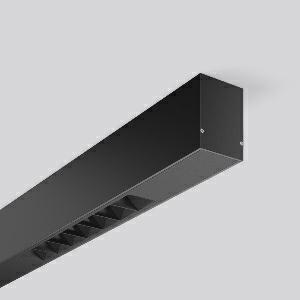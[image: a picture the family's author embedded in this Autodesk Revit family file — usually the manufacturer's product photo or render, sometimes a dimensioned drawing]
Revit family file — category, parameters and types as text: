
# Revit family: less_is_more_beamline_312488_003_3083
name_source: partatom
category: Lighting Fixtures
units: mm (PartAtom-declared; Revit-internal decimal feet)

## family parameters
Cut with Voids When Loaded = No
Host = Face
Light Source = No
Part Type = Normal
Room Calculation Point = No
Round Connector Dimension = Use Diameter
Shared = No

## types (1)
- LESS IS MORE BEAMLINE (1 x LED Modul 930, 1825 lm, 3000)
    Apparent Load = 48 VA
    CIE Flux Codes = 100 100 100 100 100
    Color Rendering = 90
    Color Temperature = 3000
    Default Elevation = 1800 mm
    Description = Series: LESS IS MORE BEAMLINE
Linear ceiling and wall luminaire for aesthetically sophisticated lighting. Luminaire with two LED light units. Housing: extruded aluminium profile, powder-coated. End cap aluminium powder-coated. LED light unit with MRS technology: Mini-Reflector-System made of metallised thermoplastic with prismatic black glare-suppressing frame for pleasant glare-free light (RUG < 10). Each LED light unit has 7 reflector elements. Wide beam light distribution. LED unit with integrated converter interchangeable and removable. Suitable for through-wiring. 
Colour: deep black, matt (RAL 9005)
Length: 1127 mm
Width: 57 mm
Height: 75 mm
Lamp: LED
Socket: without socket
Colour temperature: 3000K
Colour rendering index (CRI): 90
System power: 48 W
Rated luminous flux: 3650 lm
Luminous efficiency: 76 lm/W
Control gear: Regulated power supply
Protection class: I
Type of protection: IP 20
    Height = 75 mm
    Lamp = 1 x LED Modul 930
    Lamp Light Flux = 1825 lm
    Lamp count = 1
    Length = 1127 mm
    Lifetime = 50000 h
    Luminous efficacy = 76 lm/W
    Manufacturer = RZB
    ModVariant = No
    Model = 312488.003
    Mounting Place = Ceiling, Wall
    Mounting Type = Surface mounted
    Number of Poles = 1
    OnlyDefault = Yes
    Power Factor = 1
    Product Name = LESS IS MORE BEAMLINE
    Product group = Surface mounted LED linear luminaires
    ProductGroupID = 307
    Protection Class = Protection class I
    Protection Degree = IP 20
    RLX_Detail_Level = 1
    RLX_Emergency_Light_Flux = 0 lm
    RLX_Emergency_Type = 0
    RLX_Emergency_Type_DB = No
    RlxData = <blob elided: 29789 chars, md5=817496a8>
    Socket = socket
    Standby Power = 0 W
    System Light Flux = 3650 lm
    System Power = 48 W
    Type Comments = Product without accessories
    Type Image = 312483.003.jpg
    URL = http://relux.com
    VarID = ---
    Voltage = 230 V
    Voltage Range = 220-240 V
    Weight = 0.00 kg
    Width = 57 mm

## geometry (parser evidence)
native form markers: Blend x4, Sweep x12
no freeform markers — native parametric forms only
